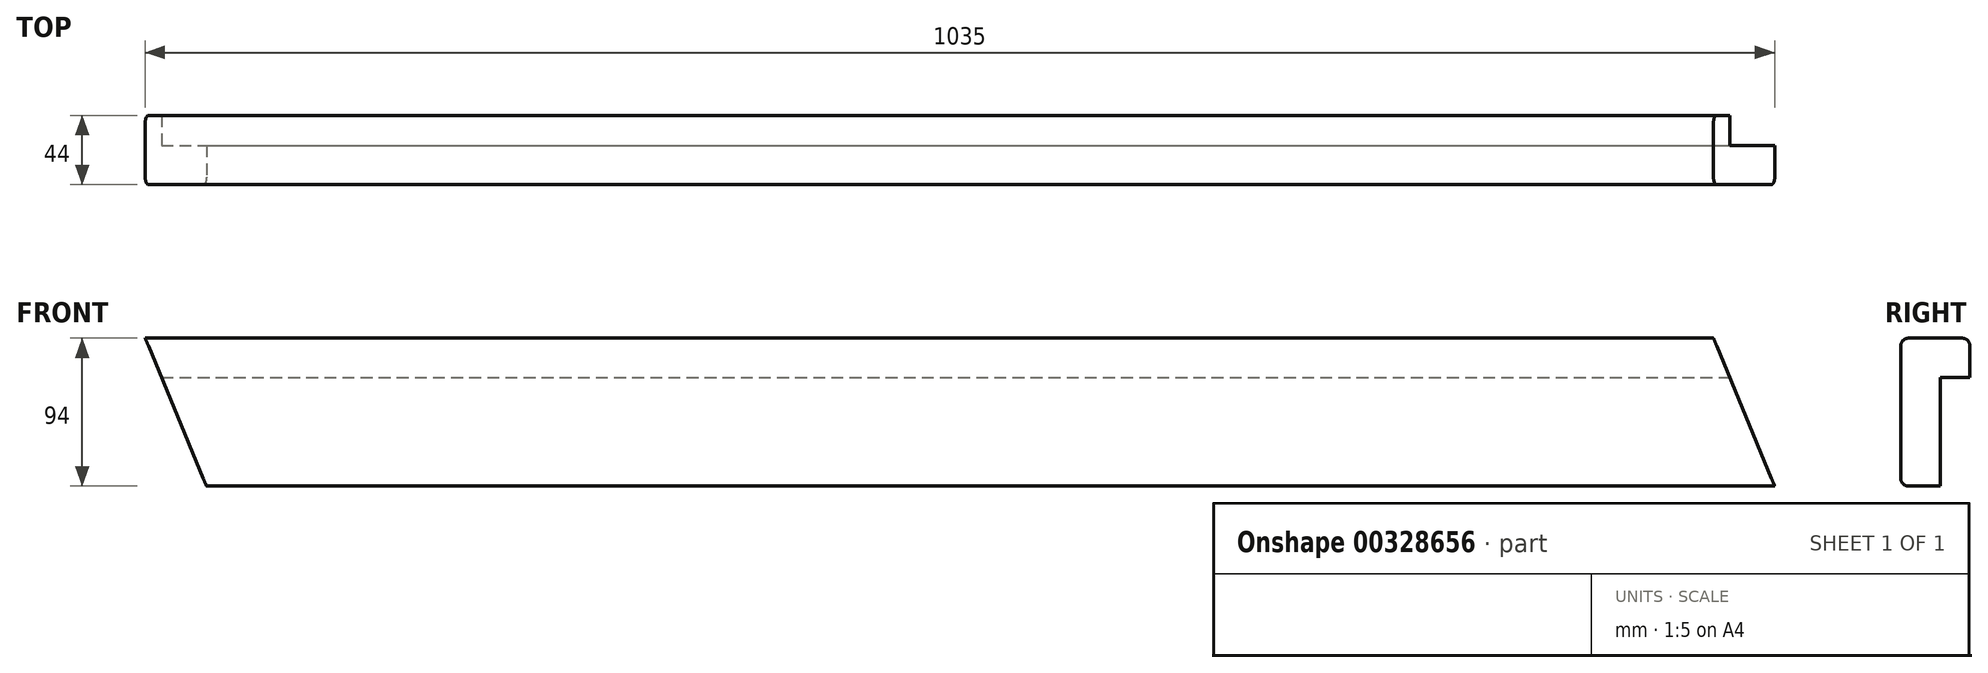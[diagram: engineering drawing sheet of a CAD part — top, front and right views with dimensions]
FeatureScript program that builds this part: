
annotation { "Feature Type Name" : "Feature", "Feature Type Description" : "" }
export const myFeature = defineFeature(function(context is Context, id is Id, definition is map)
    precondition{}
    {
        {
            var Q0;
            Q0=qCreatedBy(makeId("Front.planeOp"),FACE);
            var sketch = newSketch(context, id + "F0", { "sketchPlane" : qUnion([Q0])});
            skLineSegment(sketch, "E0.bottom", {"start": v(0, 0) * mm, "end": v(1035, 0) * mm});
            skLineSegment(sketch, "E0.top", {"start": v(38.94, -94) * mm, "end": v(1035, -94) * mm});
            skLineSegment(sketch, "E0.right", {"start": v(1035, 0) * mm, "end": v(1035, -94) * mm});
            skLineSegment(sketch, "E1", {"start": v(0, 0) * mm, "end": v(38.94, -94) * mm});
            skSolve(sketch);
        }
        {
            var Q0;
            Q0=qSketchRegion(id+"F0",true);
            extrude(context, id + "F1", {"entities" : qUnion([Q0]), "oppositeDirection" : true, "depth" : 44 * mm});
        }
        {
            var Q0;
            Q0=makeQuery(id+"F1.opExtrude","CAP_FACE",FACE,{"disambiguationData":[OSD([sQuery(id+"F0.wireOp",EDGE,"E0.bottom"),sQuery(id+"F0.wireOp",EDGE,"E0.top"),sQuery(id+"F0.wireOp",EDGE,"E0.right"),sQuery(id+"F0.wireOp",EDGE,"E1")])],"isStart":true});
            var sketch = newSketch(context, id + "F2", { "sketchPlane" : qUnion([Q0])});
            skLineSegment(sketch, "E2", {"start": v(1035, -94) * mm, "end": v(996.06, 0) * mm});
            skLineSegment(sketch, "E3", {"start": v(996.06, 0) * mm, "end": v(1035, 0) * mm});
            skLineSegment(sketch, "E4", {"start": v(1035, 0) * mm, "end": v(1035, -94) * mm});
            skSolve(sketch);
        }
        {
            var Q0;
            Q0=makeQuery(id+"F1.opExtrude","SWEPT_FACE",FACE,{"disambiguationData":[OSD([sQuery(id+"F0.wireOp",EDGE,"E0.right")])]});
            var sketch = newSketch(context, id + "F3", { "sketchPlane" : qUnion([Q0])});
            skLineSegment(sketch, "E5.bottom", {"start": v(25, -94) * mm, "end": v(44, -94) * mm});
            skLineSegment(sketch, "E5.top", {"start": v(25, -25) * mm, "end": v(44, -25) * mm});
            skLineSegment(sketch, "E5.left", {"start": v(25, -94) * mm, "end": v(25, -25) * mm});
            skLineSegment(sketch, "E5.right", {"start": v(44, -94) * mm, "end": v(44, -25) * mm});
            skSolve(sketch);
        }
        {
            var Q0;
            Q0=makeQuery(id+"F3.imprint","IMPRINT",FACE,{"disambiguationData":[TD([[makeQuery(id+"F3.imprint","IMPRINT",EDGE,{"derivedFrom":sQuery(id+"F3.wireOp",EDGE,"E5.bottom")}),-1.0]])]});
            extrude(context, id + "F4", {"entities" : qUnion([Q0]), "operationType" : NewBodyOperationType.REMOVE, "endBound" : BoundingType.THROUGH_ALL, "oppositeDirection" : true, "depth" : 25 * mm});
        }
        {
            var Q0;
            Q0=makeQuery(id+"F1.opExtrude","CAP_EDGE",EDGE,{"disambiguationData":[OSD([sQuery(id+"F0.wireOp",EDGE,"E0.bottom")])],"isStart":true});
            var Q1;
            Q1=makeQuery(id+"F1.opExtrude","CAP_EDGE",EDGE,{"disambiguationData":[OSD([sQuery(id+"F0.wireOp",EDGE,"E0.top")])],"isStart":true});
            var Q2;
            Q2=makeQuery(id+"F1.opExtrude","CAP_EDGE",EDGE,{"disambiguationData":[OSD([sQuery(id+"F0.wireOp",EDGE,"E0.bottom")])],"isStart":false});
            fillet(context, id + "F5", {"entities" : qUnion([Q0, Q1, Q2]), "radius" : 5 * mm, "tangentPropagation" : true, "allowEdgeOverflow" : false});
        }
        {
            var Q0;
            Q0=makeQuery(id+"F2.imprint","IMPRINT",FACE,{"disambiguationData":[TD([[makeQuery(id+"F2.imprint","IMPRINT",EDGE,{"derivedFrom":sQuery(id+"F2.wireOp",EDGE,"E2")}),-1.0]])]});
            extrude(context, id + "F6", {"entities" : qUnion([Q0]), "operationType" : NewBodyOperationType.REMOVE, "endBound" : BoundingType.THROUGH_ALL, "oppositeDirection" : true, "depth" : 25 * mm});
        }
    });
